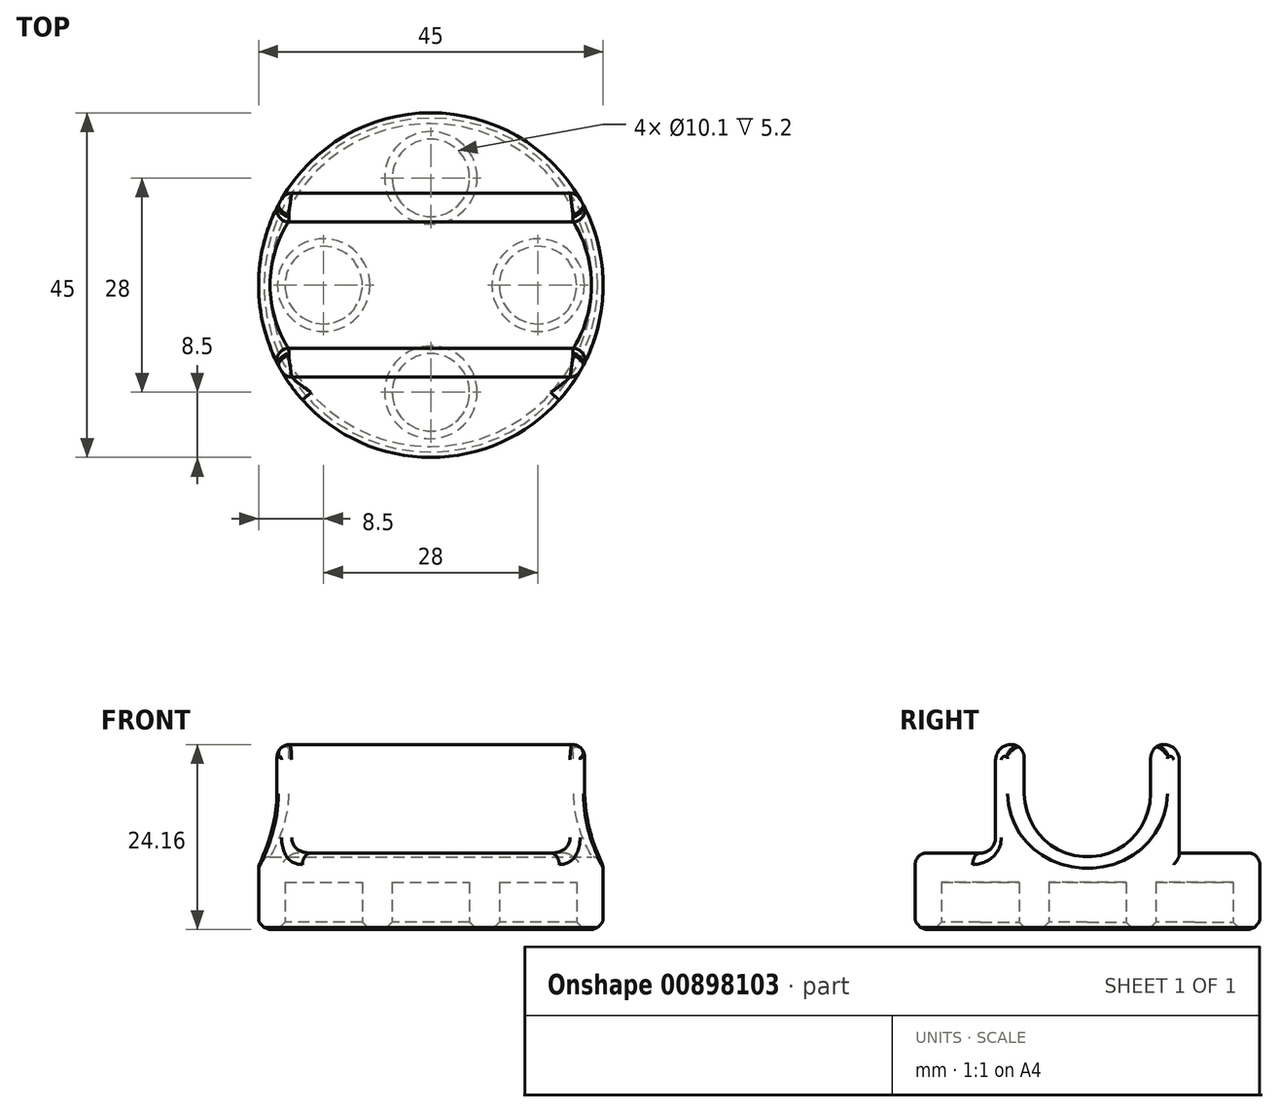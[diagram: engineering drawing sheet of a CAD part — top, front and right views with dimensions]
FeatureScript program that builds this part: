
annotation { "Feature Type Name" : "Feature", "Feature Type Description" : "" }
export const myFeature = defineFeature(function(context is Context, id is Id, definition is map)
    precondition{}
    {
        {
            var Q0;
            Q0=qCreatedBy(makeId("Top.planeOp"),FACE);
            var sketch = newSketch(context, id + "F0", { "sketchPlane" : qUnion([Q0])});
            skCircle(sketch, "E0", {"center": v(0, 0) * mm, "radius": 22.5 * mm});
            skSolve(sketch);
        }
        {
            var Q0;
            Q0=makeQuery(id+"F0.imprint","IMPRINT",FACE,{"disambiguationData":[TD([[makeQuery(id+"F0.imprint","IMPRINT",EDGE,{"derivedFrom":sQuery(id+"F0.wireOp",EDGE,"E0")}),1.0]])]});
            extrude(context, id + "F1", {"entities" : qUnion([Q0]), "depth" : 10 * mm, "offsetDistance" : 25 * mm});
        }
        {
            var Q0;
            Q0=makeQuery(id+"F1.opExtrude","CAP_FACE",FACE,{"disambiguationData":[OSD([sQuery(id+"F0.wireOp",EDGE,"E0")])],"isStart":false});
            var sketch = newSketch(context, id + "F2", { "sketchPlane" : qUnion([Q0])});
            skLineSegment(sketch, "E1.bottom", {"start": v(19.03, -12) * mm, "end": v(-19.03, -12) * mm});
            skLineSegment(sketch, "E1.top", {"start": v(19.03, 12) * mm, "end": v(-19.03, 12) * mm});
            skLineSegment(sketch, "E1.left", {"start": v(19.03, -12) * mm, "end": v(19.03, 12) * mm});
            skLineSegment(sketch, "E1.right", {"start": v(-19.03, -12) * mm, "end": v(-19.03, 12) * mm});
            skPoint(sketch, "E1.middle", {"position": v(0, 0) * mm});
            skSolve(sketch);
        }
        {
            var Q0;
            {var subQ0=sQuery(id+"F2.wireOp",EDGE,"E1.right");Q0=makeQuery(id+"F2.imprint","IMPRINT",FACE,{"disambiguationData":[TD([[makeQuery(id+"F2.imprint","IMPRINT",EDGE,{"derivedFrom":subQ0}),1.0]])]});}
            var Q1;
            Q1=makeQuery(id+"F2.imprint","IMPRINT",FACE,{"disambiguationData":[TD([[makeQuery(id+"F2.imprint","IMPRINT",EDGE,{"derivedFrom":sQuery(id+"F2.wireOp",EDGE,"E1.bottom")}),-1.0]])]});
            var Q2;
            {var subQ0=sQuery(id+"F2.wireOp",EDGE,"E1.left");Q2=makeQuery(id+"F2.imprint","IMPRINT",FACE,{"disambiguationData":[TD([[makeQuery(id+"F2.imprint","IMPRINT",EDGE,{"derivedFrom":subQ0}),-1.0]])]});}
            extrude(context, id + "F3", {"entities" : qUnion([Q0, Q1, Q2]), "operationType" : NewBodyOperationType.ADD, "depth" : 16 * mm, "offsetDistance" : 25 * mm});
        }
        {
            var Q0;
            Q0=qCreatedBy(makeId("Right.planeOp"),FACE);
            cPlane(context, id + "F4", {"entities" : qUnion([Q0]), "cplaneType" : CPlaneType.OFFSET, "offset" : (45 / 2) * mm, "width" : 150 * mm, "height" : 150 * mm});
        }
        {
            var Q0;
            Q0=qCreatedBy(id+"F4.planeOp",FACE);
            var sketch = newSketch(context, id + "F5", { "sketchPlane" : qUnion([Q0])});
            skCircle(sketch, "E2", {"center": v(0, 17.75) * mm, "radius": 8.25 * mm});
            skLineSegment(sketch, "E3", {"start": v(-22.5, 0) * mm, "end": v(-22.5, 10) * mm});
            skLineSegment(sketch, "E4", {"start": v(22.5, 10) * mm, "end": v(22.5, 0) * mm});
            skLineSegment(sketch, "E5.0", {"start": v(-12, 26) * mm, "end": v(-12, 10) * mm});
            skLineSegment(sketch, "E6.0", {"start": v(-12, 26) * mm, "end": v(12, 26) * mm});
            skLineSegment(sketch, "E7.0", {"start": v(12, 26) * mm, "end": v(12, 10) * mm});
            skLineSegment(sketch, "E8", {"start": v(-12, 26) * mm, "end": v(-6.83, 22.38) * mm});
            skLineSegment(sketch, "E9", {"start": v(12, 26) * mm, "end": v(6.83, 22.38) * mm});
            skLineSegment(sketch, "E10", {"start": v(-8.25, 17.75) * mm, "end": v(-8.25, 23.37) * mm});
            skLineSegment(sketch, "E11", {"start": v(8.25, 17.75) * mm, "end": v(8.25, 23.37) * mm});
            skSolve(sketch);
        }
        {
            var Q0;
            {var subQ0=sQuery(id+"F5.wireOp",EDGE,"E8");Q0=makeQuery(id+"F5.imprint","IMPRINT",FACE,{"disambiguationData":[TD([[makeQuery(id+"F5.imprint","IMPRINT",EDGE,{"derivedFrom":subQ0}),1.0]])]});}
            var Q1;
            {var subQ0=sQuery(id+"F5.wireOp",EDGE,"E9");Q1=makeQuery(id+"F5.imprint","IMPRINT",FACE,{"disambiguationData":[TD([[makeQuery(id+"F5.imprint","IMPRINT",EDGE,{"derivedFrom":subQ0}),-1.0]])]});}
            var Q2;
            {var subQ0=sQuery(id+"F5.wireOp",EDGE,"E2");var subQ1=makeQuery(id+"F5.imprint","INTERSECT",VERTEX,{"derivedFrom":[subQ0,sQuery(id+"F5.wireOp",EDGE,"E9")]});Q2=makeQuery(id+"F5.imprint","IMPRINT",FACE,{"disambiguationData":[TD([[makeQuery(id+"F5.imprint","IMPRINT",EDGE,{"disambiguationData":[TD([[subQ1,-1.0]])],"derivedFrom":subQ0}),1.0]])]});}
            var Q3;
            {var subQ3=sQuery(id+"F5.wireOp",EDGE,"E10");Q3=makeQuery(id+"F5.imprint","IMPRINT",FACE,{"disambiguationData":[TD([[makeQuery(id+"F5.imprint","IMPRINT",EDGE,{"derivedFrom":subQ3}),-1.0]])]});}
            var Q4;
            {var subQ3=sQuery(id+"F5.wireOp",EDGE,"E11");Q4=makeQuery(id+"F5.imprint","IMPRINT",FACE,{"disambiguationData":[TD([[makeQuery(id+"F5.imprint","IMPRINT",EDGE,{"derivedFrom":subQ3}),1.0]])]});}
            extrude(context, id + "F6", {"entities" : qUnion([Q0, Q1, Q2, Q3, Q4]), "operationType" : NewBodyOperationType.REMOVE, "endBound" : BoundingType.THROUGH_ALL, "oppositeDirection" : true, "depth" : 25 * mm, "offsetDistance" : 25 * mm});
        }
        {
            var Q0;
            Q0=makeQuery(id+"F6.boolean.opBoolean","COPY",EDGE,{"derivedFrom":makeQuery(id+"F6.opExtrude","SWEPT_EDGE",EDGE,{"disambiguationData":[OSD([sQuery(id+"F5.wireOp",EDGE,"E8"),sQuery(id+"F5.wireOp",EDGE,"E10")])]})});
            var Q1;
            Q1=makeQuery(id+"F6.boolean.opBoolean","MERGE",EDGE,{"derivedFrom":[makeQuery(id+"F3.opExtrude","CAP_EDGE",EDGE,{"disambiguationData":[OSD([sQuery(id+"F2.wireOp",EDGE,"E1.bottom")])],"isStart":false})],"fromTools":[makeQuery(id+"F6.opExtrude","SWEPT_EDGE",EDGE,{"disambiguationData":[OSD([sQuery(id+"F5.wireOp",EDGE,"E6.0"),sQuery(id+"F5.wireOp",EDGE,"E8")])]})]});
            var Q2;
            Q2=makeQuery(id+"F6.boolean.opBoolean","COPY",EDGE,{"derivedFrom":makeQuery(id+"F6.opExtrude","SWEPT_EDGE",EDGE,{"disambiguationData":[OSD([sQuery(id+"F5.wireOp",EDGE,"E9"),sQuery(id+"F5.wireOp",EDGE,"E11")])]})});
            var Q3;
            Q3=makeQuery(id+"F6.boolean.opBoolean","MERGE",EDGE,{"derivedFrom":[makeQuery(id+"F3.opExtrude","CAP_EDGE",EDGE,{"disambiguationData":[OSD([sQuery(id+"F2.wireOp",EDGE,"E1.top")])],"isStart":false})],"fromTools":[makeQuery(id+"F6.opExtrude","SWEPT_EDGE",EDGE,{"disambiguationData":[OSD([sQuery(id+"F5.wireOp",EDGE,"E6.0"),sQuery(id+"F5.wireOp",EDGE,"E9")])]})]});
            fillet(context, id + "F7", {"entities" : qUnion([Q0, Q1, Q2, Q3]), "radius" : 2 * mm, "tangentPropagation" : true, "allowEdgeOverflow" : false});
        }
        {
            var Q0;
            {var subQ0=sQuery(id+"F5.wireOp",EDGE,"E8");Q0=makeQuery(id+"F7.opFillet","BLEND_EDGE",EDGE,{"blendedFrom":[makeQuery(id+"F6.boolean.opBoolean","MERGE",EDGE,{"derivedFrom":[makeQuery(id+"F3.opExtrude","CAP_EDGE",EDGE,{"disambiguationData":[OSD([sQuery(id+"F2.wireOp",EDGE,"E1.bottom")])],"isStart":false})],"fromTools":[makeQuery(id+"F6.opExtrude","SWEPT_EDGE",EDGE,{"disambiguationData":[OSD([sQuery(id+"F5.wireOp",EDGE,"E6.0"),subQ0])]})]}),makeQuery(id+"F6.boolean.opBoolean","COPY",EDGE,{"derivedFrom":makeQuery(id+"F6.opExtrude","SWEPT_EDGE",EDGE,{"disambiguationData":[OSD([sQuery(id+"F5.wireOp",EDGE,"E2"),subQ0])]})})],"blendedInto":[]});}
            var Q1;
            {var subQ0=sQuery(id+"F5.wireOp",EDGE,"E9");Q1=makeQuery(id+"F7.opFillet","BLEND_EDGE",EDGE,{"blendedFrom":[makeQuery(id+"F6.boolean.opBoolean","MERGE",EDGE,{"derivedFrom":[makeQuery(id+"F3.opExtrude","CAP_EDGE",EDGE,{"disambiguationData":[OSD([sQuery(id+"F2.wireOp",EDGE,"E1.top")])],"isStart":false})],"fromTools":[makeQuery(id+"F6.opExtrude","SWEPT_EDGE",EDGE,{"disambiguationData":[OSD([sQuery(id+"F5.wireOp",EDGE,"E6.0"),subQ0])]})]}),makeQuery(id+"F6.boolean.opBoolean","COPY",EDGE,{"derivedFrom":makeQuery(id+"F6.opExtrude","SWEPT_EDGE",EDGE,{"disambiguationData":[OSD([sQuery(id+"F5.wireOp",EDGE,"E2"),subQ0])]})})],"blendedInto":[]});}
            fillet(context, id + "F8", {"entities" : qUnion([Q0, Q1]), "radius" : 1 * mm, "tangentPropagation" : true, "allowEdgeOverflow" : false});
        }
        {
            var Q0;
            Q0=makeQuery(id+"F3.opExtrude","CAP_EDGE",EDGE,{"disambiguationData":[OSD([sQuery(id+"F2.wireOp",EDGE,"E1.bottom")])],"isStart":true});
            var Q1;
            Q1=makeQuery(id+"F3.opExtrude","CAP_EDGE",EDGE,{"disambiguationData":[OSD([sQuery(id+"F2.wireOp",EDGE,"E1.top")])],"isStart":true});
            fillet(context, id + "F9", {"entities" : qUnion([Q0, Q1]), "radius" : 2 * mm, "tangentPropagation" : true, "allowEdgeOverflow" : false});
        }
        {
            var Q0;
            {var subQ0=sQuery(id+"F2.wireOp",EDGE,"E1.top");var subQ3=sQuery(id+"F0.wireOp",EDGE,"E0");var subQ4=makeQuery(id+"F1.opExtrude","CAP_EDGE",EDGE,{"disambiguationData":[OSD([subQ3])],"isStart":false});Q0=makeQuery(id+"F3.boolean.opBoolean","SPLIT",EDGE,{"disambiguationData":[TD([makeQuery(id+"F3.opExtrude","SWEPT_FACE",FACE,{"disambiguationData":[OSD([subQ0])]})])],"derivedFrom":subQ4});}
            var Q1;
            {var subQ0=sQuery(id+"F2.wireOp",EDGE,"E1.bottom");var subQ2=sQuery(id+"F0.wireOp",EDGE,"E0");var subQ3=makeQuery(id+"F1.opExtrude","CAP_EDGE",EDGE,{"disambiguationData":[OSD([subQ2])],"isStart":false});Q1=makeQuery(id+"F3.boolean.opBoolean","SPLIT",EDGE,{"disambiguationData":[TD([makeQuery(id+"F3.opExtrude","SWEPT_FACE",FACE,{"disambiguationData":[OSD([subQ0])]})])],"derivedFrom":subQ3});}
            var Q2;
            {var subQ0=sQuery(id+"F2.wireOp",EDGE,"E1.right");var subQ1=sQuery(id+"F2.wireOp",EDGE,"E1.bottom");var subQ2=sQuery(id+"F0.wireOp",EDGE,"E0");var subQ3=makeQuery(id+"F1.opExtrude","CAP_EDGE",EDGE,{"disambiguationData":[OSD([subQ2])],"isStart":false});var subQ4=sQuery(id+"F2.wireOp",EDGE,"E1.top");var subQ5=sQuery(id+"F2.wireOp",EDGE,"E1.left");Q2=makeQuery(id+"F9.opFillet","BLEND_EDGE",EDGE,{"disambiguationData":[OD(1.0)],"blendedFrom":[makeQuery(id+"F3.opExtrude","CAP_EDGE",EDGE,{"disambiguationData":[OSD([subQ4])],"isStart":true}),makeQuery(id+"F3.boolean.opBoolean","MERGE",FACE,{"derivedFrom":[makeQuery(id+"F1.opExtrude","SWEPT_FACE",FACE,{"disambiguationData":[OSD([subQ2])]}),makeQuery(id+"F3.opExtrude","SWEPT_FACE",FACE,{"disambiguationData":[OSD([subQ2]),TDD([makeQuery(id+"F2.imprint","IMPRINT",EDGE,{"disambiguationData":[TD([[makeQuery(id+"F2.imprint","INTERSECT",VERTEX,{"derivedFrom":[subQ3,subQ1,subQ5]}),-1.0]])],"derivedFrom":subQ3})])]}),makeQuery(id+"F3.opExtrude","SWEPT_FACE",FACE,{"disambiguationData":[OSD([subQ2]),TDD([makeQuery(id+"F2.imprint","IMPRINT",EDGE,{"disambiguationData":[TD([[makeQuery(id+"F2.imprint","INTERSECT",VERTEX,{"derivedFrom":[subQ3,subQ1,subQ0]}),1.0]])],"derivedFrom":subQ3})])]})]})],"blendedInto":[makeQuery(id+"F3.boolean.opBoolean","MERGE",FACE,{"derivedFrom":[makeQuery(id+"F1.opExtrude","SWEPT_FACE",FACE,{"disambiguationData":[OSD([subQ2])]}),makeQuery(id+"F3.opExtrude","SWEPT_FACE",FACE,{"disambiguationData":[OSD([subQ2]),TDD([makeQuery(id+"F2.imprint","IMPRINT",EDGE,{"disambiguationData":[TD([[makeQuery(id+"F2.imprint","INTERSECT",VERTEX,{"derivedFrom":[subQ3,subQ1,subQ5]}),-1.0]])],"derivedFrom":subQ3})])]}),makeQuery(id+"F3.opExtrude","SWEPT_FACE",FACE,{"disambiguationData":[OSD([subQ2]),TDD([makeQuery(id+"F2.imprint","IMPRINT",EDGE,{"disambiguationData":[TD([[makeQuery(id+"F2.imprint","INTERSECT",VERTEX,{"derivedFrom":[subQ3,subQ1,subQ0]}),1.0]])],"derivedFrom":subQ3})])]})]})]});}
            var Q3;
            {var subQ0=sQuery(id+"F2.wireOp",EDGE,"E1.right");var subQ1=sQuery(id+"F2.wireOp",EDGE,"E1.bottom");var subQ2=sQuery(id+"F0.wireOp",EDGE,"E0");var subQ3=makeQuery(id+"F1.opExtrude","CAP_EDGE",EDGE,{"disambiguationData":[OSD([subQ2])],"isStart":false});var subQ4=sQuery(id+"F2.wireOp",EDGE,"E1.top");var subQ5=sQuery(id+"F2.wireOp",EDGE,"E1.left");Q3=makeQuery(id+"F9.opFillet","BLEND_EDGE",EDGE,{"disambiguationData":[OD(0.0)],"blendedFrom":[makeQuery(id+"F3.opExtrude","CAP_EDGE",EDGE,{"disambiguationData":[OSD([subQ4])],"isStart":true}),makeQuery(id+"F3.boolean.opBoolean","MERGE",FACE,{"derivedFrom":[makeQuery(id+"F1.opExtrude","SWEPT_FACE",FACE,{"disambiguationData":[OSD([subQ2])]}),makeQuery(id+"F3.opExtrude","SWEPT_FACE",FACE,{"disambiguationData":[OSD([subQ2]),TDD([makeQuery(id+"F2.imprint","IMPRINT",EDGE,{"disambiguationData":[TD([[makeQuery(id+"F2.imprint","INTERSECT",VERTEX,{"derivedFrom":[subQ3,subQ1,subQ5]}),-1.0]])],"derivedFrom":subQ3})])]}),makeQuery(id+"F3.opExtrude","SWEPT_FACE",FACE,{"disambiguationData":[OSD([subQ2]),TDD([makeQuery(id+"F2.imprint","IMPRINT",EDGE,{"disambiguationData":[TD([[makeQuery(id+"F2.imprint","INTERSECT",VERTEX,{"derivedFrom":[subQ3,subQ1,subQ0]}),1.0]])],"derivedFrom":subQ3})])]})]})],"blendedInto":[makeQuery(id+"F3.boolean.opBoolean","MERGE",FACE,{"derivedFrom":[makeQuery(id+"F1.opExtrude","SWEPT_FACE",FACE,{"disambiguationData":[OSD([subQ2])]}),makeQuery(id+"F3.opExtrude","SWEPT_FACE",FACE,{"disambiguationData":[OSD([subQ2]),TDD([makeQuery(id+"F2.imprint","IMPRINT",EDGE,{"disambiguationData":[TD([[makeQuery(id+"F2.imprint","INTERSECT",VERTEX,{"derivedFrom":[subQ3,subQ1,subQ5]}),-1.0]])],"derivedFrom":subQ3})])]}),makeQuery(id+"F3.opExtrude","SWEPT_FACE",FACE,{"disambiguationData":[OSD([subQ2]),TDD([makeQuery(id+"F2.imprint","IMPRINT",EDGE,{"disambiguationData":[TD([[makeQuery(id+"F2.imprint","INTERSECT",VERTEX,{"derivedFrom":[subQ3,subQ1,subQ0]}),1.0]])],"derivedFrom":subQ3})])]})]})]});}
            var Q4;
            Q4=makeQuery(id+"F3.opExtrude","SWEPT_EDGE",EDGE,{"disambiguationData":[OSD([sQuery(id+"F0.wireOp",EDGE,"E0"),sQuery(id+"F2.wireOp",EDGE,"E1.top"),sQuery(id+"F2.wireOp",EDGE,"E1.right")])]});
            var Q5;
            Q5=makeQuery(id+"F3.opExtrude","SWEPT_EDGE",EDGE,{"disambiguationData":[OSD([sQuery(id+"F0.wireOp",EDGE,"E0"),sQuery(id+"F2.wireOp",EDGE,"E1.top"),sQuery(id+"F2.wireOp",EDGE,"E1.left")])]});
            var Q6;
            {var subQ0=sQuery(id+"F2.wireOp",EDGE,"E1.right");var subQ1=sQuery(id+"F2.wireOp",EDGE,"E1.bottom");var subQ2=sQuery(id+"F0.wireOp",EDGE,"E0");var subQ3=makeQuery(id+"F1.opExtrude","CAP_EDGE",EDGE,{"disambiguationData":[OSD([subQ2])],"isStart":false});var subQ5=sQuery(id+"F2.wireOp",EDGE,"E1.left");Q6=makeQuery(id+"F9.opFillet","BLEND_EDGE",EDGE,{"disambiguationData":[OD(0.0)],"blendedFrom":[makeQuery(id+"F3.opExtrude","CAP_EDGE",EDGE,{"disambiguationData":[OSD([subQ1])],"isStart":true}),makeQuery(id+"F3.boolean.opBoolean","MERGE",FACE,{"derivedFrom":[makeQuery(id+"F1.opExtrude","SWEPT_FACE",FACE,{"disambiguationData":[OSD([subQ2])]}),makeQuery(id+"F3.opExtrude","SWEPT_FACE",FACE,{"disambiguationData":[OSD([subQ2]),TDD([makeQuery(id+"F2.imprint","IMPRINT",EDGE,{"disambiguationData":[TD([[makeQuery(id+"F2.imprint","INTERSECT",VERTEX,{"derivedFrom":[subQ3,subQ1,subQ5]}),-1.0]])],"derivedFrom":subQ3})])]}),makeQuery(id+"F3.opExtrude","SWEPT_FACE",FACE,{"disambiguationData":[OSD([subQ2]),TDD([makeQuery(id+"F2.imprint","IMPRINT",EDGE,{"disambiguationData":[TD([[makeQuery(id+"F2.imprint","INTERSECT",VERTEX,{"derivedFrom":[subQ3,subQ1,subQ0]}),1.0]])],"derivedFrom":subQ3})])]})]})],"blendedInto":[makeQuery(id+"F3.boolean.opBoolean","MERGE",FACE,{"derivedFrom":[makeQuery(id+"F1.opExtrude","SWEPT_FACE",FACE,{"disambiguationData":[OSD([subQ2])]}),makeQuery(id+"F3.opExtrude","SWEPT_FACE",FACE,{"disambiguationData":[OSD([subQ2]),TDD([makeQuery(id+"F2.imprint","IMPRINT",EDGE,{"disambiguationData":[TD([[makeQuery(id+"F2.imprint","INTERSECT",VERTEX,{"derivedFrom":[subQ3,subQ1,subQ5]}),-1.0]])],"derivedFrom":subQ3})])]}),makeQuery(id+"F3.opExtrude","SWEPT_FACE",FACE,{"disambiguationData":[OSD([subQ2]),TDD([makeQuery(id+"F2.imprint","IMPRINT",EDGE,{"disambiguationData":[TD([[makeQuery(id+"F2.imprint","INTERSECT",VERTEX,{"derivedFrom":[subQ3,subQ1,subQ0]}),1.0]])],"derivedFrom":subQ3})])]})]})]});}
            var Q7;
            {var subQ0=sQuery(id+"F2.wireOp",EDGE,"E1.right");var subQ1=sQuery(id+"F2.wireOp",EDGE,"E1.bottom");var subQ2=sQuery(id+"F0.wireOp",EDGE,"E0");var subQ3=makeQuery(id+"F1.opExtrude","CAP_EDGE",EDGE,{"disambiguationData":[OSD([subQ2])],"isStart":false});var subQ5=sQuery(id+"F2.wireOp",EDGE,"E1.left");Q7=makeQuery(id+"F9.opFillet","BLEND_EDGE",EDGE,{"disambiguationData":[OD(1.0)],"blendedFrom":[makeQuery(id+"F3.opExtrude","CAP_EDGE",EDGE,{"disambiguationData":[OSD([subQ1])],"isStart":true}),makeQuery(id+"F3.boolean.opBoolean","MERGE",FACE,{"derivedFrom":[makeQuery(id+"F1.opExtrude","SWEPT_FACE",FACE,{"disambiguationData":[OSD([subQ2])]}),makeQuery(id+"F3.opExtrude","SWEPT_FACE",FACE,{"disambiguationData":[OSD([subQ2]),TDD([makeQuery(id+"F2.imprint","IMPRINT",EDGE,{"disambiguationData":[TD([[makeQuery(id+"F2.imprint","INTERSECT",VERTEX,{"derivedFrom":[subQ3,subQ1,subQ5]}),-1.0]])],"derivedFrom":subQ3})])]}),makeQuery(id+"F3.opExtrude","SWEPT_FACE",FACE,{"disambiguationData":[OSD([subQ2]),TDD([makeQuery(id+"F2.imprint","IMPRINT",EDGE,{"disambiguationData":[TD([[makeQuery(id+"F2.imprint","INTERSECT",VERTEX,{"derivedFrom":[subQ3,subQ1,subQ0]}),1.0]])],"derivedFrom":subQ3})])]})]})],"blendedInto":[makeQuery(id+"F3.boolean.opBoolean","MERGE",FACE,{"derivedFrom":[makeQuery(id+"F1.opExtrude","SWEPT_FACE",FACE,{"disambiguationData":[OSD([subQ2])]}),makeQuery(id+"F3.opExtrude","SWEPT_FACE",FACE,{"disambiguationData":[OSD([subQ2]),TDD([makeQuery(id+"F2.imprint","IMPRINT",EDGE,{"disambiguationData":[TD([[makeQuery(id+"F2.imprint","INTERSECT",VERTEX,{"derivedFrom":[subQ3,subQ1,subQ5]}),-1.0]])],"derivedFrom":subQ3})])]}),makeQuery(id+"F3.opExtrude","SWEPT_FACE",FACE,{"disambiguationData":[OSD([subQ2]),TDD([makeQuery(id+"F2.imprint","IMPRINT",EDGE,{"disambiguationData":[TD([[makeQuery(id+"F2.imprint","INTERSECT",VERTEX,{"derivedFrom":[subQ3,subQ1,subQ0]}),1.0]])],"derivedFrom":subQ3})])]})]})]});}
            var Q8;
            Q8=makeQuery(id+"F3.opExtrude","SWEPT_EDGE",EDGE,{"disambiguationData":[OSD([sQuery(id+"F0.wireOp",EDGE,"E0"),sQuery(id+"F2.wireOp",EDGE,"E1.bottom"),sQuery(id+"F2.wireOp",EDGE,"E1.right")])]});
            var Q9;
            Q9=makeQuery(id+"F3.opExtrude","SWEPT_EDGE",EDGE,{"disambiguationData":[OSD([sQuery(id+"F0.wireOp",EDGE,"E0"),sQuery(id+"F2.wireOp",EDGE,"E1.bottom"),sQuery(id+"F2.wireOp",EDGE,"E1.left")])]});
            fillet(context, id + "F10", {"entities" : qUnion([Q0, Q1, Q2, Q3, Q4, Q5, Q6, Q7, Q8, Q9]), "radius" : 1.5 * mm, "tangentPropagation" : true, "allowEdgeOverflow" : false});
        }
        {
            var Q0;
            Q0=makeQuery(id+"F1.opExtrude","CAP_EDGE",EDGE,{"disambiguationData":[OSD([sQuery(id+"F0.wireOp",EDGE,"E0")])],"isStart":true});
            chamfer(context, id + "F11", {"entities" : qUnion([Q0]), "width" : 1 * mm, "tangentPropagation" : true});
        }
        {
            var Q0;
            {var subQ0=sQuery(id+"F2.wireOp",EDGE,"E1.right");var subQ1=sQuery(id+"F2.wireOp",EDGE,"E1.bottom");var subQ2=sQuery(id+"F0.wireOp",EDGE,"E0");var subQ3=makeQuery(id+"F1.opExtrude","CAP_EDGE",EDGE,{"disambiguationData":[OSD([subQ2])],"isStart":false});var subQ5=sQuery(id+"F2.wireOp",EDGE,"E1.left");Q0=makeQuery(id+"F11.opChamfer","BLEND_EDGE",EDGE,{"blendedFrom":[makeQuery(id+"F1.opExtrude","CAP_EDGE",EDGE,{"disambiguationData":[OSD([subQ2])],"isStart":true}),makeQuery(id+"F10.opFillet","SPLIT",FACE,{"disambiguationData":[OD(4.0)],"derivedFrom":makeQuery(id+"F3.boolean.opBoolean","MERGE",FACE,{"derivedFrom":[makeQuery(id+"F1.opExtrude","SWEPT_FACE",FACE,{"disambiguationData":[OSD([subQ2])]}),makeQuery(id+"F3.opExtrude","SWEPT_FACE",FACE,{"disambiguationData":[OSD([subQ2]),TDD([makeQuery(id+"F2.imprint","IMPRINT",EDGE,{"disambiguationData":[TD([[makeQuery(id+"F2.imprint","INTERSECT",VERTEX,{"derivedFrom":[subQ3,subQ1,subQ5]}),-1.0]])],"derivedFrom":subQ3})])]}),makeQuery(id+"F3.opExtrude","SWEPT_FACE",FACE,{"disambiguationData":[OSD([subQ2]),TDD([makeQuery(id+"F2.imprint","IMPRINT",EDGE,{"disambiguationData":[TD([[makeQuery(id+"F2.imprint","INTERSECT",VERTEX,{"derivedFrom":[subQ3,subQ1,subQ0]}),1.0]])],"derivedFrom":subQ3})])]})]})})],"blendedInto":[makeQuery(id+"F10.opFillet","SPLIT",FACE,{"disambiguationData":[OD(4.0)],"derivedFrom":makeQuery(id+"F3.boolean.opBoolean","MERGE",FACE,{"derivedFrom":[makeQuery(id+"F1.opExtrude","SWEPT_FACE",FACE,{"disambiguationData":[OSD([subQ2])]}),makeQuery(id+"F3.opExtrude","SWEPT_FACE",FACE,{"disambiguationData":[OSD([subQ2]),TDD([makeQuery(id+"F2.imprint","IMPRINT",EDGE,{"disambiguationData":[TD([[makeQuery(id+"F2.imprint","INTERSECT",VERTEX,{"derivedFrom":[subQ3,subQ1,subQ5]}),-1.0]])],"derivedFrom":subQ3})])]}),makeQuery(id+"F3.opExtrude","SWEPT_FACE",FACE,{"disambiguationData":[OSD([subQ2]),TDD([makeQuery(id+"F2.imprint","IMPRINT",EDGE,{"disambiguationData":[TD([[makeQuery(id+"F2.imprint","INTERSECT",VERTEX,{"derivedFrom":[subQ3,subQ1,subQ0]}),1.0]])],"derivedFrom":subQ3})])]})]})})]});}
            fillet(context, id + "F12", {"entities" : qUnion([Q0]), "radius" : 1 * mm, "tangentPropagation" : true, "allowEdgeOverflow" : false});
        }
        {
            var Q0;
            Q0=makeQuery(id+"F1.opExtrude","CAP_FACE",FACE,{"disambiguationData":[OSD([sQuery(id+"F0.wireOp",EDGE,"E0")])],"isStart":true});
            var sketch = newSketch(context, id + "F13", { "sketchPlane" : qUnion([Q0])});
            skCircle(sketch, "E12", {"center": v(0, -14) * mm, "radius": 5.05 * mm});
            skLineSegment(sketch, "E13", {"start": v(0, 0) * mm, "end": v(0, -14) * mm});
            skCircle(sketch, "E14.1.0", {"center": v(14, 0) * mm, "radius": 5.05 * mm});
            skCircle(sketch, "E14.2.0", {"center": v(0, 14) * mm, "radius": 5.05 * mm});
            skCircle(sketch, "E14.3.0", {"center": v(-14, 0) * mm, "radius": 5.05 * mm});
            skPoint(sketch, "E14.center", {"position": v(0, 0) * mm});
            skSolve(sketch);
        }
        {
            var Q0;
            Q0=makeQuery(id+"F13.imprint","IMPRINT",FACE,{"disambiguationData":[TD([[makeQuery(id+"F13.imprint","IMPRINT",EDGE,{"derivedFrom":sQuery(id+"F13.wireOp",EDGE,"E12")}),1.0]])]});
            var Q1;
            Q1=makeQuery(id+"F13.imprint","IMPRINT",FACE,{"disambiguationData":[TD([[makeQuery(id+"F13.imprint","IMPRINT",EDGE,{"derivedFrom":sQuery(id+"F13.wireOp",EDGE,"a6ae00d4-039e-4699-a96c-ecb61de1f2aa.1.0")}),1.0]])]});
            var Q2;
            Q2=makeQuery(id+"F13.imprint","IMPRINT",FACE,{"disambiguationData":[TD([[makeQuery(id+"F13.imprint","IMPRINT",EDGE,{"derivedFrom":sQuery(id+"F13.wireOp",EDGE,"a6ae00d4-039e-4699-a96c-ecb61de1f2aa.2.0")}),1.0]])]});
            var Q3;
            Q3=makeQuery(id+"F13.imprint","IMPRINT",FACE,{"disambiguationData":[TD([[makeQuery(id+"F13.imprint","IMPRINT",EDGE,{"derivedFrom":sQuery(id+"F13.wireOp",EDGE,"E14.1.0")}),1.0]])]});
            var Q4;
            Q4=makeQuery(id+"F13.imprint","IMPRINT",FACE,{"disambiguationData":[TD([[makeQuery(id+"F13.imprint","IMPRINT",EDGE,{"derivedFrom":sQuery(id+"F13.wireOp",EDGE,"E14.2.0")}),1.0]])]});
            var Q5;
            Q5=makeQuery(id+"F13.imprint","IMPRINT",FACE,{"disambiguationData":[TD([[makeQuery(id+"F13.imprint","IMPRINT",EDGE,{"derivedFrom":sQuery(id+"F13.wireOp",EDGE,"E14.3.0")}),1.0]])]});
            extrude(context, id + "F14", {"entities" : qUnion([Q0, Q1, Q2, Q3, Q4, Q5]), "operationType" : NewBodyOperationType.REMOVE, "oppositeDirection" : true, "depth" : 6.2 * mm, "offsetDistance" : 25 * mm});
        }
        {
            var Q0;
            Q0=makeQuery(id+"F14.boolean.opBoolean","COPY",EDGE,{"derivedFrom":makeQuery(id+"F14.opExtrude","CAP_EDGE",EDGE,{"disambiguationData":[OSD([sQuery(id+"F13.wireOp",EDGE,"E12")])],"isStart":true})});
            var Q1;
            Q1=makeQuery(id+"F14.boolean.opBoolean","COPY",EDGE,{"derivedFrom":makeQuery(id+"F14.opExtrude","CAP_EDGE",EDGE,{"disambiguationData":[OSD([sQuery(id+"F13.wireOp",EDGE,"a6ae00d4-039e-4699-a96c-ecb61de1f2aa.1.0")])],"isStart":true})});
            var Q2;
            Q2=makeQuery(id+"F1.opExtrude","CAP_FACE",FACE,{"disambiguationData":[OSD([sQuery(id+"F0.wireOp",EDGE,"E0")])],"isStart":true});
            chamfer(context, id + "F15", {"entities" : qUnion([Q0, Q1, Q2]), "width" : 1 * mm, "tangentPropagation" : true});
        }
    });
